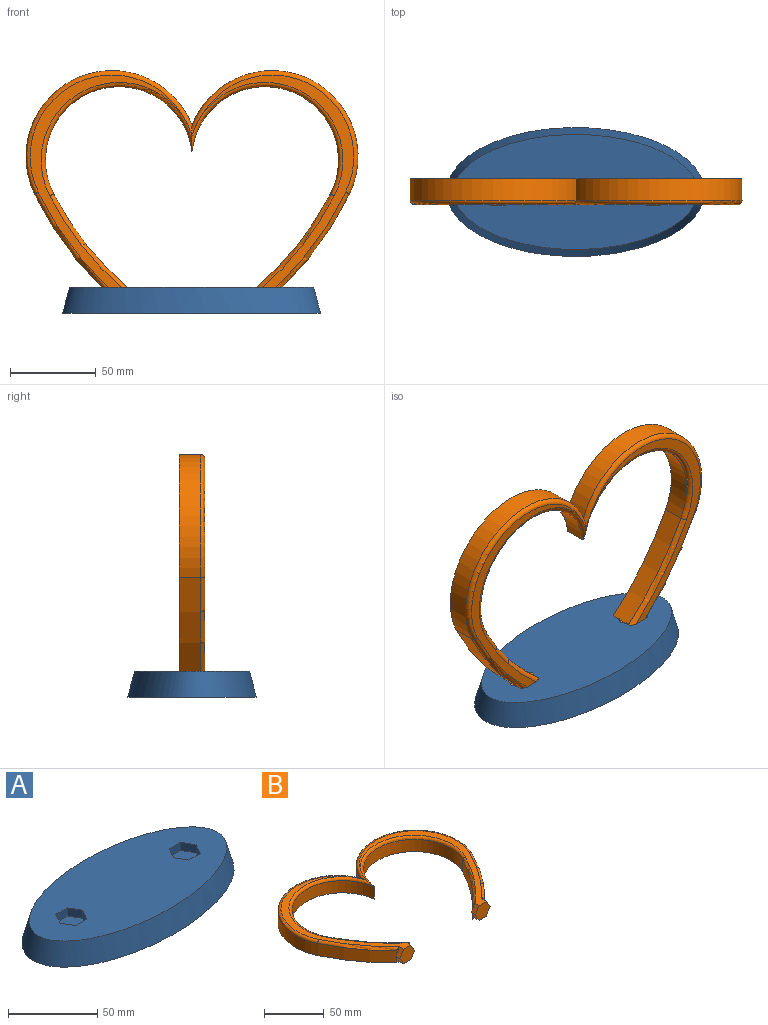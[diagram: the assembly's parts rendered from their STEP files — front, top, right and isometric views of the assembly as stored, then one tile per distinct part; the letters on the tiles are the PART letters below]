
ASSEMBLY  parts=2 mates=1
PART A: 17 faces, bbox 150x75x15 mm
  f0: plane 141.97x66.98mm, normal (0,0,1), area 7016mm2, adj f1,f3,f4,f5,f6,f7,f8,f10
  f1: bspline ~149.85x74.96mm, area 5445.9mm2, adj f0,f2
  f2: plane 150.01x75.01mm, normal (0,0,-1), area 8835.5mm2, adj f1
  f3: plane 7.7x5.5mm, normal (0.87,0.5,0), area 48.9mm2, adj f0,f4,f8,f9
  f4: plane 8.89x5.5mm, normal (0,1,0), area 48.9mm2, adj f0,f3,f5,f9
  f5: plane 7.7x5.5mm, normal (-0.87,0.5,0), area 48.9mm2, adj f0,f4,f6,f9
  f6: plane 7.7x5.5mm, normal (-0.87,-0.5,0), area 48.9mm2, adj f0,f5,f7,f9
  f7: plane 8.89x5.5mm, normal (0,-1,0), area 48.9mm2, adj f0,f6,f8,f9
  f8: plane 7.7x5.5mm, normal (0.87,-0.5,0), area 48.9mm2, adj f0,f3,f7,f9
  f9: plane 17.78x15.4mm, normal (0,0,1), area 205.4mm2, adj f3,f4,f5,f6,f7,f8
  f10: plane 7.7x5.5mm, normal (-0.87,-0.5,0), area 48.9mm2, adj f0,f11,f15,f16
  f11: plane 8.89x5.5mm, normal (0,-1,0), area 48.9mm2, adj f0,f10,f12,f16
  f12: plane 7.7x5.5mm, normal (0.87,-0.5,0), area 48.9mm2, adj f0,f11,f13,f16
  f13: plane 7.7x5.5mm, normal (0.87,0.5,0), area 48.9mm2, adj f0,f12,f14,f16
  f14: plane 8.89x5.5mm, normal (0,1,0), area 48.9mm2, adj f0,f13,f15,f16
  f15: plane 7.7x5.5mm, normal (-0.87,0.5,0), area 48.9mm2, adj f0,f10,f14,f16
  f16: plane 17.78x15.4mm, normal (0,0,1), area 205.4mm2, adj f10,f11,f12,f13,f14,f15
PART B: 41 faces, bbox 201.4x135.2x15 mm
  f0: plane 128.59x87.8mm, normal (0,0,1), area 1058.1mm2, adj f28,f29,f31,f33,f34,f35,f37
  f1: plane 5.37x3.1mm, normal (0,-1,0), area 8.3mm2, adj f11,f13,f27
  f2: plane 5.37x3.1mm, normal (0,-1,0), area 8.3mm2, adj f10,f13,f30
  f3: plane 5.33x3.07mm, normal (0,-1,0), area 6.3mm2, adj f10,f29,f33
  f4: plane 5.35x3.09mm, normal (0,-1,0), area 6.4mm2, adj f11,f28,f34
  f5: plane 5.37x3.1mm, normal (0,-1,0), area 8.3mm2, adj f8,f13,f20
  f6: plane 5.35x3.09mm, normal (0,-1,0), area 6.4mm2, adj f8,f23,f40
  f7: plane 5.33x3.07mm, normal (0,-1,0), area 6.3mm2, adj f9,f22,f36
  f8: cylinder r=190mm len=54.42mm, axis (0,0,-1), area 843.9mm2, adj f5,f6,f13,f15,f19,f40
  f9: cylinder r=180mm len=54.42mm, axis (0,0,-1), area 872.8mm2, adj f7,f13,f16,f18,f25,f36
  f10: cylinder r=180mm len=54.42mm, axis (0,0,-1), area 872.8mm2, adj f2,f3,f13,f17,f26,f33
  f11: cylinder r=190mm len=54.42mm, axis (0,0,-1), area 843.9mm2, adj f1,f4,f13,f14,f32,f34
  f12: plane 128.59x87.8mm, normal (0,0,1), area 1058.1mm2, adj f22,f23,f24,f36,f38,f39,f40
  f13: plane 193.19x131.09mm, normal (0,0,-1), area 4326.2mm2, adj f1,f2,f5,f8,f9,f10,f11,f14
  f14: cylinder r=50mm len=96.59mm, axis (0,0,-1), area 2011.6mm2, adj f11,f13,f15,f37
  f15: cylinder r=50mm len=96.59mm, axis (0,0,-1), area 2011.6mm2, adj f8,f13,f14,f39
  f16: cylinder r=42.77mm len=85.22mm, axis (0,0,-1), area 1868mm2, adj f9,f13,f17,f38
  f17: cylinder r=42.77mm len=85.22mm, axis (0,0,-1), area 1868mm2, adj f10,f13,f16,f35
  f18: plane 5.37x3.1mm, normal (0,-1,0), area 8.3mm2, adj f9,f13,f21
  f19: plane 4.25x1.23mm, normal (0,1,0), area 2.6mm2, adj f8,f20,f23
  f20: plane 7.5x5mm, normal (-0.87,0,-0.5), area 43.3mm2, adj f5,f13,f19,f23,f24
  f21: plane 7.5x5mm, normal (0.87,0,-0.5), area 43.3mm2, adj f13,f18,f22,f24,f25
  f22: plane 7.52x5.02mm, normal (0.87,0,0.5), area 43.3mm2, adj f7,f12,f21,f24,f25,f36
  f23: plane 7.51x5.5mm, normal (-0.87,0,0.5), area 43.3mm2, adj f6,f12,f19,f20,f24,f40
  f24: plane 17.32x15mm, normal (0,-1,0), area 194.9mm2, adj f12,f13,f20,f21,f22,f23
  f25: plane 4.25x1.23mm, normal (0,1,0), area 2.6mm2, adj f9,f21,f22
  f26: plane 4.25x1.23mm, normal (0,1,0), area 2.6mm2, adj f10,f29,f30
  f27: plane 7.5x5mm, normal (0.87,0,-0.5), area 43.3mm2, adj f1,f13,f28,f31,f32
  f28: plane 7.51x5.5mm, normal (0.87,0,0.5), area 43.3mm2, adj f0,f4,f27,f31,f32,f34
  f29: plane 7.52x5.02mm, normal (-0.87,0,0.5), area 43.3mm2, adj f0,f3,f26,f30,f31,f33
  f30: plane 7.5x5mm, normal (-0.87,0,-0.5), area 43.3mm2, adj f2,f13,f26,f29,f31
  f31: plane 17.32x15mm, normal (0,-1,0), area 194.9mm2, adj f0,f13,f27,f28,f29,f30
  f32: plane 4.25x1.23mm, normal (0,1,0), area 2.6mm2, adj f11,f27,f28
  f33: torus R=182.5mm, axis (0,0,1), area 271.7mm2, adj f0,f3,f10,f29,f35
  f34: torus R=187.5mm, axis (0,0,1), area 267.4mm2, adj f0,f4,f11,f28,f37
  f35: torus R=45.27mm, axis (0,0,1), area 577.7mm2, adj f0,f17,f33,f37,f38
  f36: torus R=182.5mm, axis (0,0,1), area 271.7mm2, adj f7,f9,f12,f22,f38
  f37: torus R=47.5mm, axis (0,0,1), area 626mm2, adj f0,f14,f34,f35,f39
  f38: torus R=45.27mm, axis (0,0,1), area 577.7mm2, adj f12,f16,f35,f36,f39
  f39: torus R=47.5mm, axis (0,0,1), area 626mm2, adj f12,f15,f37,f38,f40
  f40: torus R=187.5mm, axis (0,0,1), area 267.4mm2, adj f6,f8,f12,f23,f39
PLACE A rot(axis=(-1,0,0),0deg) t=(-0.13,1.87,-9.87)mm
PLACE B rot(axis=(1,0,0),90deg) t=(0.1,1.87,49.37)mm fixed
MATE planar A.f0 <-> B.f6  axis (0,0,1) through (-0.13,1.87,5.13)mm
